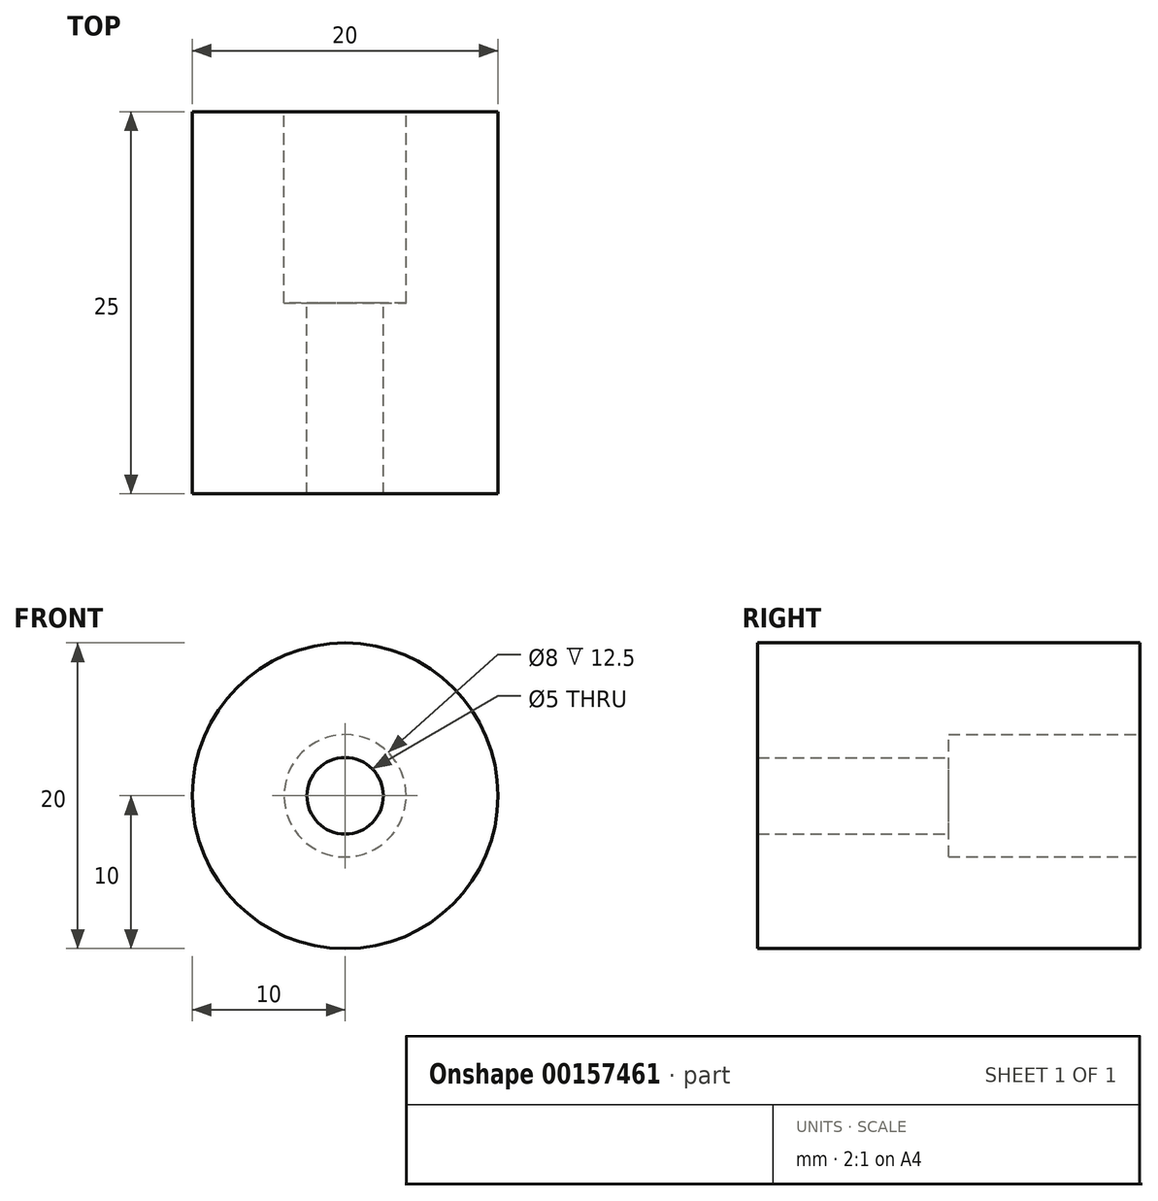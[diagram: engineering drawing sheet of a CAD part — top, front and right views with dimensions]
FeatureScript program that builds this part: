
annotation { "Feature Type Name" : "Feature", "Feature Type Description" : "" }
export const myFeature = defineFeature(function(context is Context, id is Id, definition is map)
    precondition{}
    {
        {
            var Q0;
            Q0=qCreatedBy(makeId("Front.planeOp"),FACE);
            var sketch = newSketch(context, id + "F3", { "sketchPlane" : qUnion([Q0])});
            skCircle(sketch, "E0", {"center": v(0, 0) * mm, "radius": 10 * mm});
            skCircle(sketch, "E1", {"center": v(0, 0) * mm, "radius": 4 * mm});
            skSolve(sketch);
        }
        {
            var Q0;
            Q0=makeQuery(id+"F3.imprint","IMPRINT",FACE,{"disambiguationData":[TD([[makeQuery(id+"F3.imprint","IMPRINT",EDGE,{"derivedFrom":sQuery(id+"F3.wireOp",EDGE,"E0")}),1.0]])]});
            extrude(context, id + "F0", {"entities" : qUnion([Q0]), "depth" : 12.5 * mm});
        }
        {
            var Q0;
            Q0=makeQuery(id+"F0.opExtrude","CAP_FACE",FACE,{"disambiguationData":[OSD([sQuery(id+"F3.wireOp",EDGE,"E0"),sQuery(id+"F3.wireOp",EDGE,"E1")])],"isStart":false});
            var sketch = newSketch(context, id + "F1", { "sketchPlane" : qUnion([Q0])});
            skCircle(sketch, "E2", {"center": v(0, 0) * mm, "radius": 10 * mm});
            skCircle(sketch, "E3", {"center": v(0, 0) * mm, "radius": 2.5 * mm});
            skSolve(sketch);
        }
        {
            var Q0;
            Q0=makeQuery(id+"F1.imprint","IMPRINT",FACE,{"disambiguationData":[TD([[makeQuery(id+"F1.imprint","IMPRINT",EDGE,{"derivedFrom":sQuery(id+"F1.wireOp",EDGE,"E2")}),1.0]])]});
            var Q1;
            Q1=makeQuery(id+"F1.imprint","IMPRINT",FACE,{"disambiguationData":[TD([[makeQuery(id+"F1.imprint","IMPRINT",EDGE,{"derivedFrom":sQuery(id+"F1.wireOp",EDGE,"E3")}),-1.0]])]});
            extrude(context, id + "F2", {"entities" : qUnion([Q0, Q1]), "operationType" : NewBodyOperationType.ADD, "depth" : 12.5 * mm});
        }
    });
